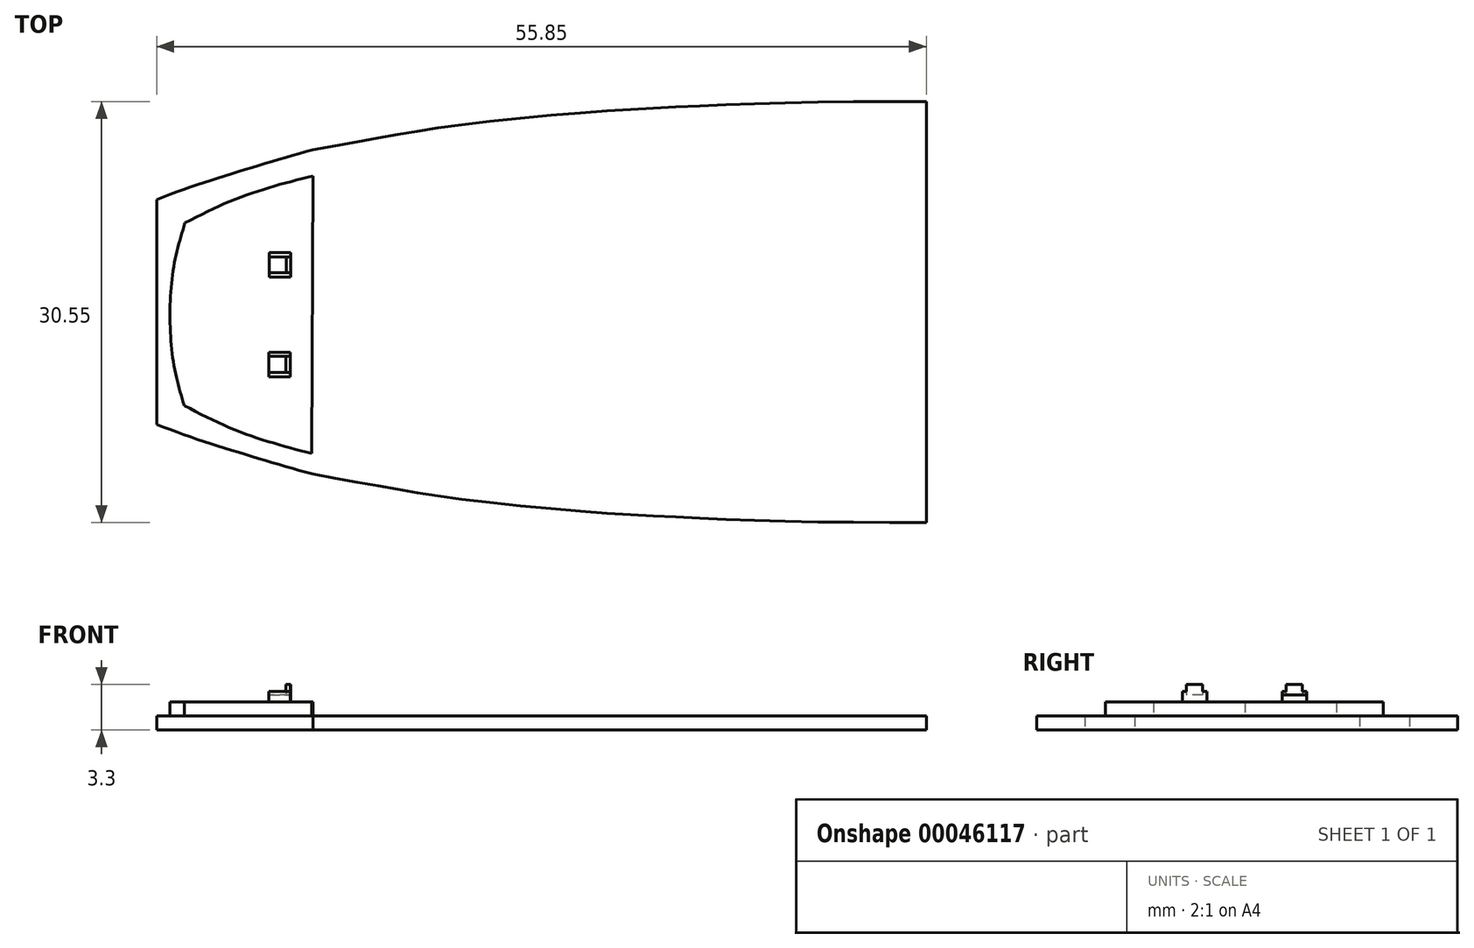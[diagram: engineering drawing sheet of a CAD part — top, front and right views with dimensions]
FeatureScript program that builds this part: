
annotation { "Feature Type Name" : "Feature", "Feature Type Description" : "" }
export const myFeature = defineFeature(function(context is Context, id is Id, definition is map)
    precondition{}
    {
        {
            var Q0;
            Q0=qCreatedBy(makeId("Top.planeOp"),FACE);
            var sketch = newSketch(context, id + "F0", { "sketchPlane" : qUnion([Q0])});
            skFitSpline(sketch, "E0", {"points": [v(-83.07, 65.02) * mm, v(-77.7, 65.98) * mm, v(-72.76, 66.78) * mm, v(-62.97, 67.76) * mm, v(-56.68, 68.13) * mm, v(-47.91, 68.45) * mm, v(-33.56, 68.5) * mm, v(-23.68, 68.4) * mm], "startDerivative": vector(48.1, 8.64) * mm, "endDerivative": vector(59.07, -0.66) * mm});
            skFitSpline(sketch, "E1", {"points": [v(-83.07, 65.02) * mm, v(-85.88, 64.21) * mm, v(-88.66, 63.37) * mm, v(-91.54, 62.45) * mm, v(-94.4, 61.41) * mm], "startDerivative": vector(-11.37, -3.2) * mm, "endDerivative": vector(-11.25, -4.21) * mm});
            skFitSpline(sketch, "E2.MirrorCS", {"points": [v(-83.07, 41.48) * mm, v(-85.88, 42.28) * mm, v(-88.66, 43.13) * mm, v(-91.54, 44.05) * mm, v(-94.4, 45.08) * mm], "startDerivative": vector(-11.37, 3.2) * mm, "endDerivative": vector(-11.25, 4.21) * mm});
            skFitSpline(sketch, "E3.MirrorCS", {"points": [v(-83.07, 41.48) * mm, v(-77.7, 40.51) * mm, v(-72.76, 39.72) * mm, v(-62.97, 38.74) * mm, v(-56.68, 38.37) * mm, v(-47.91, 38.04) * mm, v(-33.56, 38) * mm, v(-23.68, 38.1) * mm], "startDerivative": vector(48.1, -8.64) * mm, "endDerivative": vector(59.07, 0.66) * mm});
            skLineSegment(sketch, "E4", {"start": v(-94.4, 61.41) * mm, "end": v(-94.4, 45.08) * mm});
            skLineSegment(sketch, "E5", {"start": v(-38.55, 68.52) * mm, "end": v(-38.55, 37.98) * mm});
            skSolve(sketch);
        }
        {
            var Q0;
            Q0 = qSketchRegion(id + "F0", true);
            extrude(context, id + "F1", {"entities" : qUnion([Q0]), "depth" : 1.02 * mm, "offsetDistance" : 25.4 * mm});
        }
        {
            var Q0;
            Q0=makeQuery(id+"F1.opExtrude","CAP_FACE",FACE,{"disambiguationData":[OSD([sQuery(id+"F0.wireOp",EDGE,"E0"),sQuery(id+"F0.wireOp",EDGE,"E1"),sQuery(id+"F0.wireOp",EDGE,"E2.MirrorCS"),sQuery(id+"F0.wireOp",EDGE,"E3.MirrorCS"),sQuery(id+"F0.wireOp",EDGE,"E4"),sQuery(id+"F0.wireOp",EDGE,"E5")])],"isStart":false});
            var sketch = newSketch(context, id + "F2", { "sketchPlane" : qUnion([Q0])});
            skFitSpline(sketch, "E6", {"points": [v(-83.06, 63.13) * mm, v(-86, 62.34) * mm, v(-89.05, 61.29) * mm, v(-92.35, 59.72) * mm], "startDerivative": vector(-9.18, -2.33) * mm, "endDerivative": vector(-9.43, -4.77) * mm});
            skFitSpline(sketch, "E7", {"points": [v(-92.35, 59.72) * mm, v(-92.86, 57.91) * mm, v(-93.28, 55.75) * mm, v(-93.45, 53.1) * mm], "startDerivative": vector(-1.75, -5.8) * mm, "endDerivative": vector(-0.27, -7.48) * mm});
            skFitSpline(sketch, "E8.MirrorCS", {"points": [v(-83.14, 42.97) * mm, v(-86.07, 43.78) * mm, v(-89.12, 44.86) * mm, v(-92.4, 46.45) * mm], "startDerivative": vector(-9.16, 2.4) * mm, "endDerivative": vector(-9.4, 4.85) * mm});
            skFitSpline(sketch, "E9.MirrorCS", {"points": [v(-92.4, 46.45) * mm, v(-92.9, 48.26) * mm, v(-93.3, 50.43) * mm, v(-93.45, 53.1) * mm], "startDerivative": vector(-1.7, 5.8) * mm, "endDerivative": vector(-0.2, 7.49) * mm});
            skLineSegment(sketch, "E10", {"start": v(-83.06, 63.13) * mm, "end": v(-83.14, 42.97) * mm});
            skSolve(sketch);
        }
        {
            var Q0;
            Q0 = qSketchRegion(id + "F2", true);
            extrude(context, id + "F3", {"entities" : qUnion([Q0]), "operationType" : NewBodyOperationType.ADD, "depth" : 1.02 * mm, "offsetDistance" : 25.4 * mm});
        }
        {
            var Q0;
            Q0=makeQuery(id+"F3.opExtrude","CAP_FACE",FACE,{"disambiguationData":[OSD([sQuery(id+"F2.wireOp",EDGE,"E6"),sQuery(id+"F2.wireOp",EDGE,"E7"),sQuery(id+"F2.wireOp",EDGE,"E8.MirrorCS"),sQuery(id+"F2.wireOp",EDGE,"E9.MirrorCS"),sQuery(id+"F2.wireOp",EDGE,"E10")])],"isStart":false});
            var sketch = newSketch(context, id + "F4", { "sketchPlane" : qUnion([Q0])});
            skLineSegment(sketch, "E11.bottom", {"start": v(-86.25, 50.33) * mm, "end": v(-84.7, 50.33) * mm});
            skLineSegment(sketch, "E11.top", {"start": v(-86.25, 48.55) * mm, "end": v(-84.7, 48.55) * mm});
            skLineSegment(sketch, "E11.left", {"start": v(-86.25, 50.33) * mm, "end": v(-86.25, 48.55) * mm});
            skLineSegment(sketch, "E11.right", {"start": v(-84.7, 50.33) * mm, "end": v(-84.7, 48.55) * mm});
            skLineSegment(sketch, "E12", {"start": v(-93.45, 53.1) * mm, "end": v(-80.37, 53.04) * mm});
            skLineSegment(sketch, "E13.MirrorCS", {"start": v(-86.23, 55.8) * mm, "end": v(-84.69, 55.78) * mm});
            skLineSegment(sketch, "E14.MirrorCS", {"start": v(-86.23, 55.8) * mm, "end": v(-86.22, 57.58) * mm});
            skLineSegment(sketch, "E15.MirrorCS", {"start": v(-84.69, 55.78) * mm, "end": v(-84.67, 57.56) * mm});
            skLineSegment(sketch, "E16.MirrorCS", {"start": v(-86.22, 57.58) * mm, "end": v(-84.67, 57.56) * mm});
            skSolve(sketch);
        }
        {
            var Q0;
            Q0 = qSketchRegion(id + "F4", true);
            extrude(context, id + "F5", {"entities" : qUnion([Q0]), "operationType" : NewBodyOperationType.ADD, "depth" : 0.5 * mm, "offsetDistance" : 25.4 * mm});
        }
        {
            var Q0;
            Q0=makeQuery(id+"F5.opExtrude","CAP_FACE",FACE,{"disambiguationData":[OSD([sQuery(id+"F4.wireOp",EDGE,"E11.bottom"),sQuery(id+"F4.wireOp",EDGE,"E11.top"),sQuery(id+"F4.wireOp",EDGE,"E11.left"),sQuery(id+"F4.wireOp",EDGE,"E11.right")])],"isStart":false});
            var sketch = newSketch(context, id + "F6", { "sketchPlane" : qUnion([Q0])});
            skLineSegment(sketch, "E17", {"start": v(-86.25, 48.85) * mm, "end": v(-84.7, 48.85) * mm});
            skLineSegment(sketch, "E18.MirrorCS", {"start": v(-86.25, 50.02) * mm, "end": v(-84.7, 50.02) * mm});
            skLineSegment(sketch, "E19", {"start": v(-85.04, 50.02) * mm, "end": v(-85.04, 48.85) * mm});
            skLineSegment(sketch, "E20", {"start": v(-86.25, 50.02) * mm, "end": v(-86.25, 50.33) * mm});
            skLineSegment(sketch, "E21", {"start": v(-86.25, 50.33) * mm, "end": v(-84.7, 50.33) * mm});
            skLineSegment(sketch, "E22", {"start": v(-84.7, 50.33) * mm, "end": v(-84.7, 48.55) * mm});
            skLineSegment(sketch, "E23", {"start": v(-84.7, 48.55) * mm, "end": v(-86.25, 48.55) * mm});
            skLineSegment(sketch, "E24", {"start": v(-86.25, 48.55) * mm, "end": v(-86.25, 48.85) * mm});
            skLineSegment(sketch, "E25", {"start": v(-86.22, 56.08) * mm, "end": v(-84.67, 56.08) * mm});
            skLineSegment(sketch, "E26.MirrorCS", {"start": v(-86.22, 57.25) * mm, "end": v(-84.67, 57.25) * mm});
            skLineSegment(sketch, "E27", {"start": v(-85, 57.25) * mm, "end": v(-85, 56.08) * mm});
            skLineSegment(sketch, "E28", {"start": v(-86.22, 57.25) * mm, "end": v(-86.22, 57.56) * mm});
            skLineSegment(sketch, "E29", {"start": v(-86.22, 57.56) * mm, "end": v(-84.67, 57.56) * mm});
            skLineSegment(sketch, "E30", {"start": v(-84.67, 57.56) * mm, "end": v(-84.67, 55.78) * mm});
            skLineSegment(sketch, "E31", {"start": v(-84.67, 55.78) * mm, "end": v(-86.22, 55.78) * mm});
            skLineSegment(sketch, "E32", {"start": v(-86.22, 55.78) * mm, "end": v(-86.22, 56.08) * mm});
            skSolve(sketch);
        }
        {
            var Q0;
            {var subQ3=sQuery(id+"F6.wireOp",EDGE,"E27");Q0=makeQuery(id+"F6.imprint","IMPRINT",FACE,{"disambiguationData":[TD([[makeQuery(id+"F6.imprint","IMPRINT",EDGE,{"derivedFrom":subQ3}),1.0]])]});}
            var Q1;
            {var subQ3=sQuery(id+"F6.wireOp",EDGE,"E19");Q1=makeQuery(id+"F6.imprint","IMPRINT",FACE,{"disambiguationData":[TD([[makeQuery(id+"F6.imprint","IMPRINT",EDGE,{"derivedFrom":subQ3}),1.0]])]});}
            extrude(context, id + "F7", {"entities" : qUnion([Q0, Q1]), "operationType" : NewBodyOperationType.ADD, "depth" : 0.76 * mm, "offsetDistance" : 25.4 * mm});
        }
        {
            var Q0;
            {var subQ1=sQuery(id+"F6.wireOp",EDGE,"E28");Q0=makeQuery(id+"F6.imprint","IMPRINT",FACE,{"disambiguationData":[TD([[makeQuery(id+"F6.imprint","IMPRINT",EDGE,{"derivedFrom":subQ1}),-1.0]])]});}
            var Q1;
            {var subQ3=sQuery(id+"F6.wireOp",EDGE,"E31");Q1=makeQuery(id+"F6.imprint","IMPRINT",FACE,{"disambiguationData":[TD([[makeQuery(id+"F6.imprint","IMPRINT",EDGE,{"derivedFrom":subQ3}),-1.0]])]});}
            var Q2;
            {var subQ1=sQuery(id+"F6.wireOp",EDGE,"E20");Q2=makeQuery(id+"F6.imprint","IMPRINT",FACE,{"disambiguationData":[TD([[makeQuery(id+"F6.imprint","IMPRINT",EDGE,{"derivedFrom":subQ1}),1.0]])]});}
            var Q3;
            {var subQ0=sQuery(id+"F6.wireOp",EDGE,"E23");Q3=makeQuery(id+"F6.imprint","IMPRINT",FACE,{"disambiguationData":[TD([[makeQuery(id+"F6.imprint","IMPRINT",EDGE,{"derivedFrom":subQ0}),1.0]])]});}
            extrude(context, id + "F8", {"entities" : qUnion([Q0, Q1, Q2, Q3]), "operationType" : NewBodyOperationType.ADD, "depth" : 0.25 * mm, "offsetDistance" : 25.4 * mm});
        }
    });
